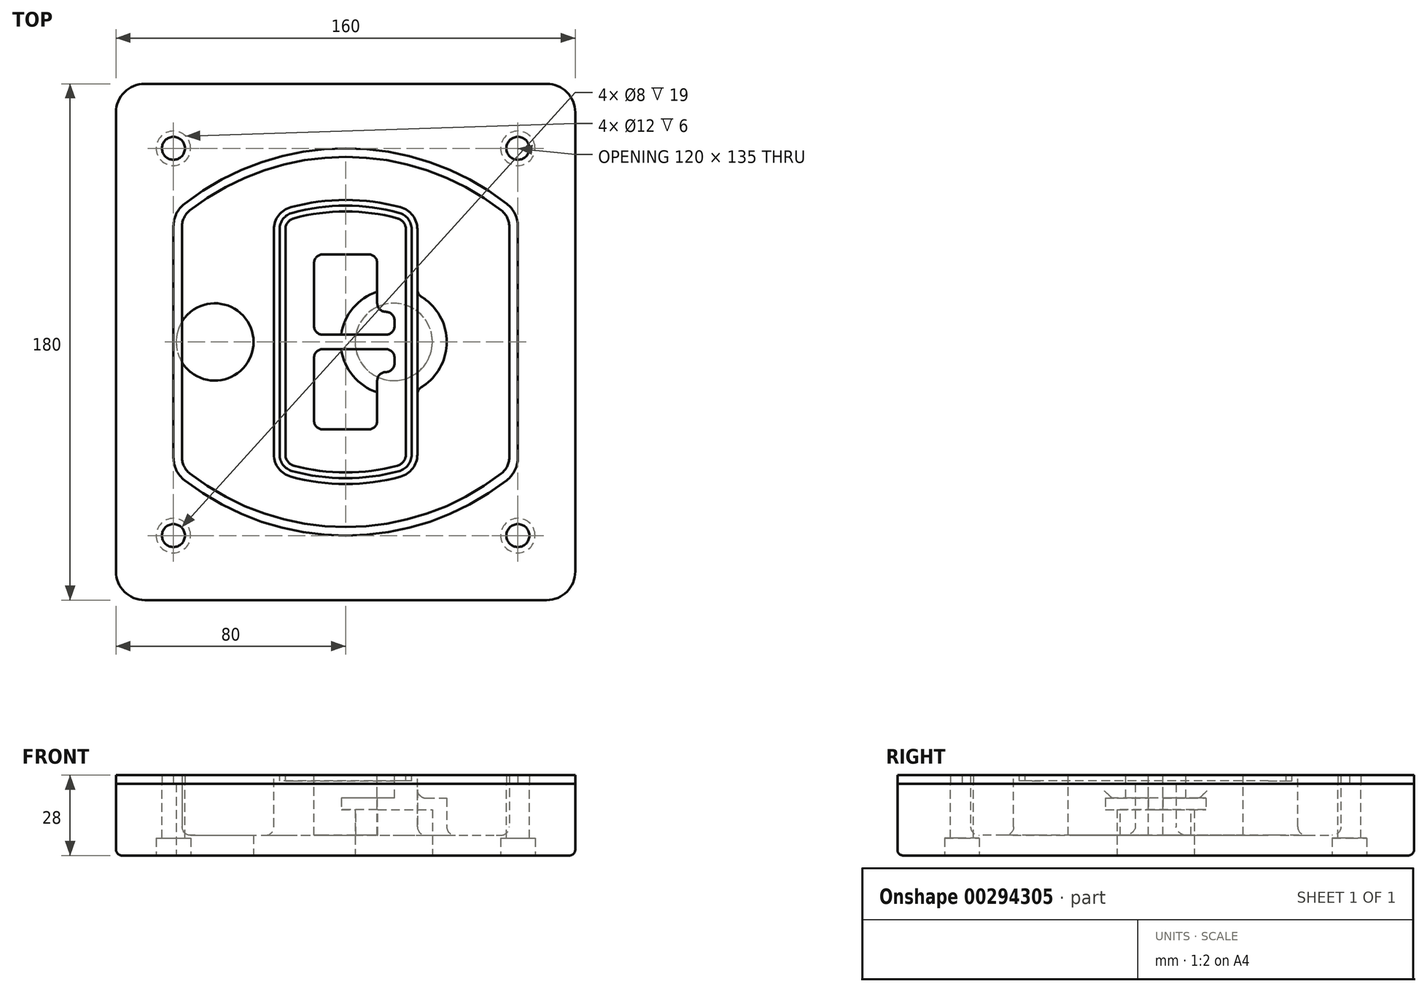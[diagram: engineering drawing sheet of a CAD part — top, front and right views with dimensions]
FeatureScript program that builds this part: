
annotation { "Feature Type Name" : "Feature", "Feature Type Description" : "" }
export const myFeature = defineFeature(function(context is Context, id is Id, definition is map)
    precondition{}
    {
        {
            var Q0;
            Q0=qCreatedBy(makeId("Top.planeOp"),FACE);
            var sketch = newSketch(context, id + "F0", { "sketchPlane" : qUnion([Q0])});
            skPoint(sketch, "E0.rect.middle", {"position": v(0, 0) * mm});
            skLineSegment(sketch, "E1.bottom", {"start": v(-70, -90) * mm, "end": v(70, -90) * mm});
            skLineSegment(sketch, "E1.top", {"start": v(-70, 90) * mm, "end": v(70, 90) * mm});
            skLineSegment(sketch, "E1.left", {"start": v(-80, -80) * mm, "end": v(-80, 80) * mm});
            skLineSegment(sketch, "E1.right", {"start": v(80, -80) * mm, "end": v(80, 80) * mm});
            skLineSegment(sketch, "E2", {"start": v(-80, 90) * mm, "end": v(80, -90) * mm, "construction": true});
            skLineSegment(sketch, "E3", {"start": v(80, 90) * mm, "end": v(-80, -90) * mm, "construction": true});
            skCircle(sketch, "E4", {"center": v(-60, 67.5) * mm, "radius": 4 * mm});
            skCircle(sketch, "E5", {"center": v(60, 67.5) * mm, "radius": 4 * mm});
            skCircle(sketch, "E6", {"center": v(60, -67.5) * mm, "radius": 4 * mm});
            skCircle(sketch, "E7", {"center": v(-60, -67.5) * mm, "radius": 4 * mm});
            skLineSegment(sketch, "E8", {"start": v(-60, 67.5) * mm, "end": v(60, 67.5) * mm, "construction": true});
            skLineSegment(sketch, "E9", {"start": v(60, 67.5) * mm, "end": v(60, -67.5) * mm, "construction": true});
            skLineSegment(sketch, "E10", {"start": v(60, -67.5) * mm, "end": v(-60, -67.5) * mm, "construction": true});
            skLineSegment(sketch, "E11", {"start": v(-60, -67.5) * mm, "end": v(-60, 67.5) * mm, "construction": true});
            skLineSegment(sketch, "E12", {"start": v(-60, 40.3) * mm, "end": v(-60, -40.3) * mm});
            skLineSegment(sketch, "E13", {"start": v(60, 40.3) * mm, "end": v(60, -40.3) * mm});
            skArc(sketch, "E14", {"start": v(56.15, 48.18) * mm, "mid": v(0, 67.5) * mm, "end": v(-56.15, 48.18) * mm});
            skArc(sketch, "E15", {"start": v(-56.15, -48.18) * mm, "mid": v(0, -67.5) * mm, "end": v(56.15, -48.18) * mm});
            skLineSegment(sketch, "E16", {"start": v(-60, 0) * mm, "end": v(60, 0) * mm, "construction": true});
            skPoint(sketch, "E17.visualSharp", {"position": v(-60, -45) * mm});
            skArc(sketch, "E17.filletArc", {"start": v(-60, -40.3) * mm, "mid": v(-58.99, -44.68) * mm, "end": v(-56.15, -48.18) * mm});
            skPoint(sketch, "E18.visualSharp", {"position": v(-60, 45) * mm});
            skArc(sketch, "E18.filletArc", {"start": v(-56.15, 48.18) * mm, "mid": v(-58.99, 44.68) * mm, "end": v(-60, 40.3) * mm});
            skPoint(sketch, "E19.visualSharp", {"position": v(60, 45) * mm});
            skArc(sketch, "E19.filletArc", {"start": v(60, 40.3) * mm, "mid": v(58.99, 44.68) * mm, "end": v(56.15, 48.18) * mm});
            skPoint(sketch, "E20.visualSharp", {"position": v(60, -45) * mm});
            skArc(sketch, "E20.filletArc", {"start": v(56.15, -48.18) * mm, "mid": v(58.99, -44.68) * mm, "end": v(60, -40.3) * mm});
            skPoint(sketch, "E21.visualSharp", {"position": v(-80, 90) * mm});
            skArc(sketch, "E21.filletArc", {"start": v(-70, 90) * mm, "mid": v(-77.07, 87.07) * mm, "end": v(-80, 80) * mm});
            skPoint(sketch, "E22.visualSharp", {"position": v(80, 90) * mm});
            skArc(sketch, "E22.filletArc", {"start": v(80, 80) * mm, "mid": v(77.07, 87.07) * mm, "end": v(70, 90) * mm});
            skPoint(sketch, "E23.visualSharp", {"position": v(80, -90) * mm});
            skArc(sketch, "E23.filletArc", {"start": v(70, -90) * mm, "mid": v(77.07, -87.07) * mm, "end": v(80, -80) * mm});
            skPoint(sketch, "E24.visualSharp", {"position": v(-80, -90) * mm});
            skArc(sketch, "E24.filletArc", {"start": v(-80, -80) * mm, "mid": v(-77.07, -87.07) * mm, "end": v(-70, -90) * mm});
            skArc(sketch, "E25.0", {"start": v(57, 40.3) * mm, "mid": v(56.3, 43.36) * mm, "end": v(54.3, 45.81) * mm});
            skLineSegment(sketch, "E25.1", {"start": v(57, 40.3) * mm, "end": v(57, -40.3) * mm});
            skArc(sketch, "E25.2", {"start": v(54.3, -45.81) * mm, "mid": v(56.3, -43.36) * mm, "end": v(57, -40.3) * mm});
            skArc(sketch, "E25.3", {"start": v(-54.3, -45.81) * mm, "mid": v(0, -64.5) * mm, "end": v(54.3, -45.81) * mm});
            skArc(sketch, "E25.4", {"start": v(-57, -40.3) * mm, "mid": v(-56.3, -43.36) * mm, "end": v(-54.3, -45.81) * mm});
            skArc(sketch, "E25.5", {"start": v(54.3, 45.81) * mm, "mid": v(0, 64.5) * mm, "end": v(-54.3, 45.81) * mm});
            skLineSegment(sketch, "E25.6", {"start": v(-57, 40.3) * mm, "end": v(-57, -40.3) * mm});
            skArc(sketch, "E25.7", {"start": v(-54.3, 45.81) * mm, "mid": v(-56.3, 43.36) * mm, "end": v(-57, 40.3) * mm});
            skArc(sketch, "E26.0", {"start": v(-58.62, 51.33) * mm, "mid": v(-62.58, 46.43) * mm, "end": v(-64, 40.3) * mm});
            skArc(sketch, "E26.1", {"start": v(58.62, 51.33) * mm, "mid": v(0, 71.5) * mm, "end": v(-58.62, 51.33) * mm});
            skArc(sketch, "E26.2", {"start": v(64, 40.3) * mm, "mid": v(62.58, 46.43) * mm, "end": v(58.62, 51.33) * mm});
            skLineSegment(sketch, "E26.3", {"start": v(64, 40.3) * mm, "end": v(64, -40.3) * mm});
            skArc(sketch, "E26.4", {"start": v(58.62, -51.33) * mm, "mid": v(62.58, -46.43) * mm, "end": v(64, -40.3) * mm});
            skLineSegment(sketch, "E26.5", {"start": v(-64, 40.3) * mm, "end": v(-64, -40.3) * mm});
            skArc(sketch, "E26.6", {"start": v(-58.62, -51.33) * mm, "mid": v(0, -71.5) * mm, "end": v(58.62, -51.33) * mm});
            skArc(sketch, "E26.7", {"start": v(-64, -40.3) * mm, "mid": v(-62.58, -46.43) * mm, "end": v(-58.62, -51.33) * mm});
            skSolve(sketch);
        }
        {
            var Q0;
            Q0=makeQuery(id+"F0.imprint","IMPRINT",FACE,{"disambiguationData":[TD([[makeQuery(id+"F0.imprint","IMPRINT",EDGE,{"derivedFrom":sQuery(id+"F0.wireOp",EDGE,"E1.bottom")}),1.0]])]});
            var Q1;
            Q1=makeQuery(id+"F0.imprint","IMPRINT",FACE,{"disambiguationData":[TD([[makeQuery(id+"F0.imprint","IMPRINT",EDGE,{"derivedFrom":sQuery(id+"F0.wireOp",EDGE,"E12")}),1.0]])]});
            var Q2;
            Q2=makeQuery(id+"F0.imprint","IMPRINT",FACE,{"disambiguationData":[TD([[makeQuery(id+"F0.imprint","IMPRINT",EDGE,{"derivedFrom":sQuery(id+"F0.wireOp",EDGE,"E25.0")}),1.0]])]});
            var Q3;
            Q3=makeQuery(id+"F0.imprint","IMPRINT",FACE,{"disambiguationData":[TD([[makeQuery(id+"F0.imprint","IMPRINT",EDGE,{"derivedFrom":sQuery(id+"F0.wireOp",EDGE,"E12")}),-1.0]])]});
            extrude(context, id + "F1", {"entities" : qUnion([Q0, Q1, Q2, Q3]), "oppositeDirection" : true, "depth" : 25 * mm});
        }
        {
            var Q0;
            Q0=makeQuery(id+"F0.imprint","IMPRINT",FACE,{"disambiguationData":[TD([[makeQuery(id+"F0.imprint","IMPRINT",EDGE,{"derivedFrom":sQuery(id+"F0.wireOp",EDGE,"E12")}),1.0]])]});
            extrude(context, id + "F2", {"entities" : qUnion([Q0]), "operationType" : NewBodyOperationType.ADD, "depth" : 3 * mm});
        }
        {
            var Q0;
            Q0=makeQuery(id+"F0.imprint","IMPRINT",FACE,{"disambiguationData":[TD([[makeQuery(id+"F0.imprint","IMPRINT",EDGE,{"derivedFrom":sQuery(id+"F0.wireOp",EDGE,"E25.0")}),1.0]])]});
            extrude(context, id + "F3", {"entities" : qUnion([Q0]), "operationType" : NewBodyOperationType.REMOVE, "oppositeDirection" : true, "depth" : 18 * mm});
        }
        {
            var Q0;
            Q0=makeQuery(id+"F2.opExtrude","CAP_FACE",FACE,{"disambiguationData":[OSD([sQuery(id+"F0.wireOp",EDGE,"E12"),sQuery(id+"F0.wireOp",EDGE,"E13"),sQuery(id+"F0.wireOp",EDGE,"E14"),sQuery(id+"F0.wireOp",EDGE,"E15"),sQuery(id+"F0.wireOp",EDGE,"E17.filletArc"),sQuery(id+"F0.wireOp",EDGE,"E18.filletArc"),sQuery(id+"F0.wireOp",EDGE,"E19.filletArc"),sQuery(id+"F0.wireOp",EDGE,"E20.filletArc"),sQuery(id+"F0.wireOp",EDGE,"E25.0"),sQuery(id+"F0.wireOp",EDGE,"E25.1"),sQuery(id+"F0.wireOp",EDGE,"E25.2"),sQuery(id+"F0.wireOp",EDGE,"E25.3"),sQuery(id+"F0.wireOp",EDGE,"E25.4"),sQuery(id+"F0.wireOp",EDGE,"E25.5"),sQuery(id+"F0.wireOp",EDGE,"E25.6"),sQuery(id+"F0.wireOp",EDGE,"E25.7")])],"isStart":false});
            var sketch = newSketch(context, id + "F4", { "sketchPlane" : qUnion([Q0])});
            skArc(sketch, "E27.0", {"start": v(-19.08, -46.97) * mm, "mid": v(0, -49.5) * mm, "end": v(19.08, -46.97) * mm});
            skArc(sketch, "E28.0", {"start": v(19.08, 46.97) * mm, "mid": v(0, 49.5) * mm, "end": v(-19.08, 46.97) * mm});
            skLineSegment(sketch, "E29", {"start": v(-25, 39.25) * mm, "end": v(-25, -39.25) * mm});
            skLineSegment(sketch, "E30", {"start": v(25, 39.25) * mm, "end": v(25, -39.25) * mm});
            skLineSegment(sketch, "E31", {"start": v(-25, 45.1) * mm, "end": v(25, 45.1) * mm, "construction": true});
            skLineSegment(sketch, "E32", {"start": v(-25, -45.1) * mm, "end": v(25, -45.1) * mm, "construction": true});
            skPoint(sketch, "E33.visualSharp", {"position": v(-25, 45.1) * mm});
            skArc(sketch, "E33.filletArc", {"start": v(-19.08, 46.97) * mm, "mid": v(-23.35, 44.11) * mm, "end": v(-25, 39.25) * mm});
            skPoint(sketch, "E34.visualSharp", {"position": v(25, 45.1) * mm});
            skArc(sketch, "E34.filletArc", {"start": v(25, 39.25) * mm, "mid": v(23.35, 44.11) * mm, "end": v(19.08, 46.97) * mm});
            skPoint(sketch, "E35.visualSharp", {"position": v(25, -45.1) * mm});
            skArc(sketch, "E35.filletArc", {"start": v(19.08, -46.97) * mm, "mid": v(23.35, -44.11) * mm, "end": v(25, -39.25) * mm});
            skPoint(sketch, "E36.visualSharp", {"position": v(-25, -45.1) * mm});
            skArc(sketch, "E36.filletArc", {"start": v(-25, -39.25) * mm, "mid": v(-23.35, -44.11) * mm, "end": v(-19.08, -46.97) * mm});
            skArc(sketch, "E37.0", {"start": v(54.3, 45.81) * mm, "mid": v(0, 64.5) * mm, "end": v(-54.3, 45.81) * mm});
            skArc(sketch, "E37.1", {"start": v(-54.3, 45.81) * mm, "mid": v(-56.3, 43.36) * mm, "end": v(-57, 40.3) * mm});
            skLineSegment(sketch, "E37.2", {"start": v(-57, 40.3) * mm, "end": v(-57, -40.3) * mm});
            skArc(sketch, "E37.3", {"start": v(-57, -40.3) * mm, "mid": v(-56.3, -43.36) * mm, "end": v(-54.3, -45.81) * mm});
            skArc(sketch, "E37.4", {"start": v(-54.3, -45.81) * mm, "mid": v(0, -64.5) * mm, "end": v(54.3, -45.81) * mm});
            skArc(sketch, "E37.5", {"start": v(54.3, -45.81) * mm, "mid": v(56.3, -43.36) * mm, "end": v(57, -40.3) * mm});
            skLineSegment(sketch, "E37.6", {"start": v(57, 40.3) * mm, "end": v(57, -40.3) * mm});
            skArc(sketch, "E37.7", {"start": v(57, 40.3) * mm, "mid": v(56.3, 43.36) * mm, "end": v(54.3, 45.81) * mm});
            skLineSegment(sketch, "E38.0", {"start": v(23, 39.25) * mm, "end": v(23, -39.25) * mm});
            skArc(sketch, "E38.1", {"start": v(18.56, -45.04) * mm, "mid": v(21.76, -42.9) * mm, "end": v(23, -39.25) * mm});
            skArc(sketch, "E38.2", {"start": v(-18.56, -45.04) * mm, "mid": v(0, -47.5) * mm, "end": v(18.56, -45.04) * mm});
            skArc(sketch, "E38.3", {"start": v(-23, -39.25) * mm, "mid": v(-21.76, -42.9) * mm, "end": v(-18.56, -45.04) * mm});
            skLineSegment(sketch, "E38.4", {"start": v(-23, 39.25) * mm, "end": v(-23, -39.25) * mm});
            skArc(sketch, "E38.5", {"start": v(23, 39.25) * mm, "mid": v(21.76, 42.9) * mm, "end": v(18.56, 45.04) * mm});
            skArc(sketch, "E38.6", {"start": v(-18.56, 45.04) * mm, "mid": v(-21.76, 42.9) * mm, "end": v(-23, 39.25) * mm});
            skArc(sketch, "E38.7", {"start": v(18.56, 45.04) * mm, "mid": v(0, 47.5) * mm, "end": v(-18.56, 45.04) * mm});
            skArc(sketch, "E39.0", {"start": v(21, 39.25) * mm, "mid": v(20.18, 41.68) * mm, "end": v(18.04, 43.1) * mm});
            skLineSegment(sketch, "E39.1", {"start": v(21, 39.25) * mm, "end": v(21, -39.25) * mm});
            skArc(sketch, "E39.2", {"start": v(18.04, -43.1) * mm, "mid": v(20.18, -41.68) * mm, "end": v(21, -39.25) * mm});
            skArc(sketch, "E39.3", {"start": v(-18.04, -43.1) * mm, "mid": v(0, -45.5) * mm, "end": v(18.04, -43.1) * mm});
            skArc(sketch, "E39.4", {"start": v(-21, -39.25) * mm, "mid": v(-20.18, -41.68) * mm, "end": v(-18.04, -43.1) * mm});
            skArc(sketch, "E39.5", {"start": v(18.04, 43.1) * mm, "mid": v(0, 45.5) * mm, "end": v(-18.04, 43.1) * mm});
            skLineSegment(sketch, "E39.6", {"start": v(-21, 39.25) * mm, "end": v(-21, -39.25) * mm});
            skArc(sketch, "E39.7", {"start": v(-18.04, 43.1) * mm, "mid": v(-20.18, 41.68) * mm, "end": v(-21, 39.25) * mm});
            skLineSegment(sketch, "E40", {"start": v(-25, 0) * mm, "end": v(25, 0) * mm, "construction": true});
            skLineSegment(sketch, "E41", {"start": v(-11, 5.5) * mm, "end": v(-11, 27.5) * mm});
            skLineSegment(sketch, "E42", {"start": v(-8, 30.5) * mm, "end": v(8, 30.5) * mm});
            skLineSegment(sketch, "E43", {"start": v(11, 27.5) * mm, "end": v(11, 13.5) * mm});
            skLineSegment(sketch, "E44", {"start": v(14, 10.5) * mm, "end": v(14, 10.5) * mm});
            skLineSegment(sketch, "E45", {"start": v(17, 7.5) * mm, "end": v(17, 5.5) * mm});
            skLineSegment(sketch, "E46", {"start": v(14, 2.5) * mm, "end": v(-8, 2.5) * mm});
            skPoint(sketch, "E47.visualSharp", {"position": v(-11, 30.5) * mm});
            skArc(sketch, "E47.filletArc", {"start": v(-8, 30.5) * mm, "mid": v(-10.12, 29.62) * mm, "end": v(-11, 27.5) * mm});
            skPoint(sketch, "E48.visualSharp", {"position": v(11, 30.5) * mm});
            skArc(sketch, "E48.filletArc", {"start": v(11, 27.5) * mm, "mid": v(10.12, 29.62) * mm, "end": v(8, 30.5) * mm});
            skPoint(sketch, "E49.visualSharp", {"position": v(11, 10.5) * mm});
            skArc(sketch, "E49.filletArc", {"start": v(11, 13.5) * mm, "mid": v(11.88, 11.38) * mm, "end": v(14, 10.5) * mm});
            skPoint(sketch, "E50.visualSharp", {"position": v(17, 10.5) * mm});
            skArc(sketch, "E50.filletArc", {"start": v(17, 7.5) * mm, "mid": v(16.12, 9.62) * mm, "end": v(14, 10.5) * mm});
            skPoint(sketch, "E51.visualSharp", {"position": v(17, 2.5) * mm});
            skArc(sketch, "E51.filletArc", {"start": v(14, 2.5) * mm, "mid": v(16.12, 3.38) * mm, "end": v(17, 5.5) * mm});
            skPoint(sketch, "E52.visualSharp", {"position": v(-11, 2.5) * mm});
            skArc(sketch, "E52.filletArc", {"start": v(-11, 5.5) * mm, "mid": v(-10.12, 3.38) * mm, "end": v(-8, 2.5) * mm});
            skLineSegment(sketch, "E53.0.MirrorCS", {"start": v(14, -2.5) * mm, "end": v(-8, -2.5) * mm});
            skArc(sketch, "E54.0.MirrorCS", {"start": v(-11, -5.5) * mm, "mid": v(-10.12, -3.38) * mm, "end": v(-8, -2.5) * mm});
            skLineSegment(sketch, "E55.0.MirrorCS", {"start": v(-11, -5.5) * mm, "end": v(-11, -27.5) * mm});
            skArc(sketch, "E56.0.MirrorCS", {"start": v(-8, -30.5) * mm, "mid": v(-10.12, -29.62) * mm, "end": v(-11, -27.5) * mm});
            skLineSegment(sketch, "E57.0.MirrorCS", {"start": v(-8, -30.5) * mm, "end": v(8, -30.5) * mm});
            skArc(sketch, "E58.0.MirrorCS", {"start": v(11, -27.5) * mm, "mid": v(10.12, -29.62) * mm, "end": v(8, -30.5) * mm});
            skLineSegment(sketch, "E59.0.MirrorCS", {"start": v(11, -27.5) * mm, "end": v(11, -13.5) * mm});
            skArc(sketch, "E60.0.MirrorCS", {"start": v(11, -13.5) * mm, "mid": v(11.88, -11.38) * mm, "end": v(14, -10.5) * mm});
            skArc(sketch, "E61.0.MirrorCS", {"start": v(17, -7.5) * mm, "mid": v(16.12, -9.62) * mm, "end": v(14, -10.5) * mm});
            skLineSegment(sketch, "E62.0.MirrorCS", {"start": v(17, -7.5) * mm, "end": v(17, -5.5) * mm});
            skArc(sketch, "E63.0.MirrorCS", {"start": v(14, -2.5) * mm, "mid": v(16.12, -3.38) * mm, "end": v(17, -5.5) * mm});
            skSolve(sketch);
        }
        {
            var Q0;
            Q0=makeQuery(id+"F4.imprint","IMPRINT",FACE,{"disambiguationData":[TD([[makeQuery(id+"F4.imprint","IMPRINT",EDGE,{"derivedFrom":sQuery(id+"F4.wireOp",EDGE,"E27.0")}),1.0]])]});
            var Q1;
            Q1=makeQuery(id+"F4.imprint","IMPRINT",FACE,{"disambiguationData":[TD([[makeQuery(id+"F4.imprint","IMPRINT",EDGE,{"derivedFrom":sQuery(id+"F4.wireOp",EDGE,"E38.0")}),-1.0]])]});
            var Q2;
            Q2=makeQuery(id+"F4.imprint","IMPRINT",FACE,{"disambiguationData":[TD([[makeQuery(id+"F4.imprint","IMPRINT",EDGE,{"derivedFrom":sQuery(id+"F4.wireOp",EDGE,"E39.0")}),1.0]])]});
            extrude(context, id + "F5", {"entities" : qUnion([Q0, Q1, Q2]), "operationType" : NewBodyOperationType.ADD, "endBound" : BoundingType.UP_TO_NEXT, "oppositeDirection" : true, "depth" : 25 * mm});
        }
        {
            var Q0;
            Q0=makeQuery(id+"F4.imprint","IMPRINT",FACE,{"disambiguationData":[TD([[makeQuery(id+"F4.imprint","IMPRINT",EDGE,{"derivedFrom":sQuery(id+"F4.wireOp",EDGE,"E38.0")}),-1.0]])]});
            extrude(context, id + "F6", {"entities" : qUnion([Q0]), "operationType" : NewBodyOperationType.REMOVE, "oppositeDirection" : true, "depth" : 2 * mm});
        }
        {
            var Q0;
            Q0=makeQuery(id+"F1.opExtrude","CAP_FACE",FACE,{"disambiguationData":[OSD([sQuery(id+"F0.wireOp",EDGE,"E1.bottom"),sQuery(id+"F0.wireOp",EDGE,"E1.top"),sQuery(id+"F0.wireOp",EDGE,"E1.left"),sQuery(id+"F0.wireOp",EDGE,"E1.right"),sQuery(id+"F0.wireOp",EDGE,"E4"),sQuery(id+"F0.wireOp",EDGE,"E5"),sQuery(id+"F0.wireOp",EDGE,"E6"),sQuery(id+"F0.wireOp",EDGE,"E7"),sQuery(id+"F0.wireOp",EDGE,"E21.filletArc"),sQuery(id+"F0.wireOp",EDGE,"E22.filletArc"),sQuery(id+"F0.wireOp",EDGE,"E23.filletArc"),sQuery(id+"F0.wireOp",EDGE,"E24.filletArc")])],"isStart":false});
            var sketch = newSketch(context, id + "F7", { "sketchPlane" : qUnion([Q0])});
            skCircle(sketch, "E64", {"center": v(16.76, 0) * mm, "radius": 13.47 * mm});
            skCircle(sketch, "E65", {"center": v(-45.56, 0) * mm, "radius": 13.47 * mm});
            skLineSegment(sketch, "E66", {"start": v(80, 0) * mm, "end": v(-80, 0) * mm});
            skCircle(sketch, "E67", {"center": v(16.76, 0) * mm, "radius": 18.47 * mm});
            skCircle(sketch, "E68", {"center": v(60, -67.5) * mm, "radius": 6 * mm});
            skCircle(sketch, "E69", {"center": v(-60, -67.5) * mm, "radius": 6 * mm});
            skCircle(sketch, "E70", {"center": v(-60, 67.5) * mm, "radius": 6 * mm});
            skCircle(sketch, "E71", {"center": v(60, 67.5) * mm, "radius": 6 * mm});
            skSolve(sketch);
        }
        {
            var Q0;
            {var subQ1=sQuery(id+"F7.wireOp",EDGE,"E66");var subQ4=sQuery(id+"F7.wireOp",EDGE,"E64");var subQ6=makeQuery(id+"F7.imprint","INTERSECT",VERTEX,{"disambiguationData":[OD(0.0)],"derivedFrom":[subQ4,subQ1]});Q0=makeQuery(id+"F7.imprint","IMPRINT",FACE,{"disambiguationData":[TD([[makeQuery(id+"F7.imprint","IMPRINT",EDGE,{"disambiguationData":[TD([[subQ6,-1.0]])],"derivedFrom":subQ4}),-1.0]])]});}
            var Q1;
            {var subQ0=sQuery(id+"F7.wireOp",EDGE,"E66");var subQ1=sQuery(id+"F7.wireOp",EDGE,"E64");var subQ3=makeQuery(id+"F7.imprint","INTERSECT",VERTEX,{"disambiguationData":[OD(0.0)],"derivedFrom":[subQ1,subQ0]});Q1=makeQuery(id+"F7.imprint","IMPRINT",FACE,{"disambiguationData":[TD([[makeQuery(id+"F7.imprint","IMPRINT",EDGE,{"disambiguationData":[TD([[subQ3,-1.0]])],"derivedFrom":subQ1}),1.0]])]});}
            var Q2;
            {var subQ0=sQuery(id+"F7.wireOp",EDGE,"E66");var subQ1=sQuery(id+"F7.wireOp",EDGE,"E64");var subQ3=makeQuery(id+"F7.imprint","INTERSECT",VERTEX,{"disambiguationData":[OD(0.0)],"derivedFrom":[subQ1,subQ0]});Q2=makeQuery(id+"F7.imprint","IMPRINT",FACE,{"disambiguationData":[TD([[makeQuery(id+"F7.imprint","IMPRINT",EDGE,{"disambiguationData":[TD([[subQ3,1.0]])],"derivedFrom":subQ1}),1.0]])]});}
            var Q3;
            {var subQ1=sQuery(id+"F7.wireOp",EDGE,"E66");var subQ4=sQuery(id+"F7.wireOp",EDGE,"E64");var subQ6=makeQuery(id+"F7.imprint","INTERSECT",VERTEX,{"disambiguationData":[OD(0.0)],"derivedFrom":[subQ4,subQ1]});Q3=makeQuery(id+"F7.imprint","IMPRINT",FACE,{"disambiguationData":[TD([[makeQuery(id+"F7.imprint","IMPRINT",EDGE,{"disambiguationData":[TD([[subQ6,1.0]])],"derivedFrom":subQ4}),-1.0]])]});}
            extrude(context, id + "F8", {"entities" : qUnion([Q0, Q1, Q2, Q3]), "operationType" : NewBodyOperationType.ADD, "oppositeDirection" : true, "depth" : 20 * mm});
        }
        {
            var Q0;
            {var subQ0=sQuery(id+"F7.wireOp",EDGE,"E66");var subQ1=sQuery(id+"F7.wireOp",EDGE,"E64");var subQ3=makeQuery(id+"F7.imprint","INTERSECT",VERTEX,{"disambiguationData":[OD(0.0)],"derivedFrom":[subQ1,subQ0]});Q0=makeQuery(id+"F7.imprint","IMPRINT",FACE,{"disambiguationData":[TD([[makeQuery(id+"F7.imprint","IMPRINT",EDGE,{"disambiguationData":[TD([[subQ3,-1.0]])],"derivedFrom":subQ1}),1.0]])]});}
            var Q1;
            {var subQ0=sQuery(id+"F7.wireOp",EDGE,"E66");var subQ1=sQuery(id+"F7.wireOp",EDGE,"E64");var subQ3=makeQuery(id+"F7.imprint","INTERSECT",VERTEX,{"disambiguationData":[OD(0.0)],"derivedFrom":[subQ1,subQ0]});Q1=makeQuery(id+"F7.imprint","IMPRINT",FACE,{"disambiguationData":[TD([[makeQuery(id+"F7.imprint","IMPRINT",EDGE,{"disambiguationData":[TD([[subQ3,1.0]])],"derivedFrom":subQ1}),1.0]])]});}
            extrude(context, id + "F9", {"entities" : qUnion([Q0, Q1]), "operationType" : NewBodyOperationType.REMOVE, "oppositeDirection" : true, "depth" : 16 * mm});
        }
        {
            var Q0;
            {var subQ0=sQuery(id+"F7.wireOp",EDGE,"E66");var subQ1=sQuery(id+"F7.wireOp",EDGE,"E65");var subQ3=makeQuery(id+"F7.imprint","INTERSECT",VERTEX,{"disambiguationData":[OD(0.0)],"derivedFrom":[subQ1,subQ0]});Q0=makeQuery(id+"F7.imprint","IMPRINT",FACE,{"disambiguationData":[TD([[makeQuery(id+"F7.imprint","IMPRINT",EDGE,{"disambiguationData":[TD([[subQ3,-1.0]])],"derivedFrom":subQ1}),1.0]])]});}
            var Q1;
            {var subQ0=sQuery(id+"F7.wireOp",EDGE,"E66");var subQ1=sQuery(id+"F7.wireOp",EDGE,"E65");var subQ3=makeQuery(id+"F7.imprint","INTERSECT",VERTEX,{"disambiguationData":[OD(0.0)],"derivedFrom":[subQ1,subQ0]});Q1=makeQuery(id+"F7.imprint","IMPRINT",FACE,{"disambiguationData":[TD([[makeQuery(id+"F7.imprint","IMPRINT",EDGE,{"disambiguationData":[TD([[subQ3,1.0]])],"derivedFrom":subQ1}),1.0]])]});}
            extrude(context, id + "F10", {"entities" : qUnion([Q0, Q1]), "operationType" : NewBodyOperationType.REMOVE, "oppositeDirection" : true, "depth" : 25 * mm});
        }
        {
            var Q0;
            Q0=makeQuery(id+"F7.imprint","IMPRINT",FACE,{"disambiguationData":[TD([[makeQuery(id+"F7.imprint","IMPRINT",EDGE,{"derivedFrom":sQuery(id+"F7.wireOp",EDGE,"E68")}),1.0]])]});
            var Q1;
            Q1=makeQuery(id+"F7.imprint","IMPRINT",FACE,{"disambiguationData":[TD([[makeQuery(id+"F7.imprint","IMPRINT",EDGE,{"derivedFrom":makeQuery(id+"F1.opExtrude","CAP_EDGE",EDGE,{"disambiguationData":[OSD([sQuery(id+"F0.wireOp",EDGE,"E5")])],"isStart":false})}),-1.0]])]});
            var Q2;
            Q2=makeQuery(id+"F7.imprint","IMPRINT",FACE,{"disambiguationData":[TD([[makeQuery(id+"F7.imprint","IMPRINT",EDGE,{"derivedFrom":sQuery(id+"F7.wireOp",EDGE,"E69")}),1.0]])]});
            var Q3;
            Q3=makeQuery(id+"F7.imprint","IMPRINT",FACE,{"disambiguationData":[TD([[makeQuery(id+"F7.imprint","IMPRINT",EDGE,{"derivedFrom":makeQuery(id+"F1.opExtrude","CAP_EDGE",EDGE,{"disambiguationData":[OSD([sQuery(id+"F0.wireOp",EDGE,"E4")])],"isStart":false})}),-1.0]])]});
            var Q4;
            Q4=makeQuery(id+"F7.imprint","IMPRINT",FACE,{"disambiguationData":[TD([[makeQuery(id+"F7.imprint","IMPRINT",EDGE,{"derivedFrom":sQuery(id+"F7.wireOp",EDGE,"E70")}),1.0]])]});
            var Q5;
            Q5=makeQuery(id+"F7.imprint","IMPRINT",FACE,{"disambiguationData":[TD([[makeQuery(id+"F7.imprint","IMPRINT",EDGE,{"derivedFrom":makeQuery(id+"F1.opExtrude","CAP_EDGE",EDGE,{"disambiguationData":[OSD([sQuery(id+"F0.wireOp",EDGE,"E7")])],"isStart":false})}),-1.0]])]});
            var Q6;
            Q6=makeQuery(id+"F7.imprint","IMPRINT",FACE,{"disambiguationData":[TD([[makeQuery(id+"F7.imprint","IMPRINT",EDGE,{"derivedFrom":sQuery(id+"F7.wireOp",EDGE,"E71")}),1.0]])]});
            var Q7;
            Q7=makeQuery(id+"F7.imprint","IMPRINT",FACE,{"disambiguationData":[TD([[makeQuery(id+"F7.imprint","IMPRINT",EDGE,{"derivedFrom":makeQuery(id+"F1.opExtrude","CAP_EDGE",EDGE,{"disambiguationData":[OSD([sQuery(id+"F0.wireOp",EDGE,"E6")])],"isStart":false})}),-1.0]])]});
            extrude(context, id + "F11", {"entities" : qUnion([Q0, Q1, Q2, Q3, Q4, Q5, Q6, Q7]), "operationType" : NewBodyOperationType.REMOVE, "oppositeDirection" : true, "depth" : 6 * mm});
        }
        {
            var Q0;
            Q0=makeQuery(id+"F9.boolean.opBoolean","COPY",FACE,{"derivedFrom":makeQuery(id+"F9.opExtrude","CAP_FACE",FACE,{"disambiguationData":[OSD([sQuery(id+"F7.wireOp",EDGE,"E64")])],"isStart":false})});
            var sketch = newSketch(context, id + "F12", { "sketchPlane" : qUnion([Q0])});
            skArc(sketch, "E72.0", {"start": v(11, 17.55) * mm, "mid": v(2.57, 11.82) * mm, "end": v(-1.54, 2.5) * mm});
            skArc(sketch, "E72.1", {"start": v(-1.54, -2.5) * mm, "mid": v(2.57, -11.82) * mm, "end": v(11, -17.55) * mm});
            skLineSegment(sketch, "E73", {"start": v(-1.54, -2.5) * mm, "end": v(14, -2.5) * mm});
            skLineSegment(sketch, "E74.0", {"start": v(14, 2.5) * mm, "end": v(-1.54, 2.5) * mm});
            skArc(sketch, "E74.1", {"start": v(14, 2.5) * mm, "mid": v(16.12, 3.38) * mm, "end": v(17, 5.5) * mm});
            skLineSegment(sketch, "E74.2", {"start": v(17, 7.5) * mm, "end": v(17, 5.5) * mm});
            skArc(sketch, "E74.3", {"start": v(17, 7.5) * mm, "mid": v(16.12, 9.62) * mm, "end": v(14, 10.5) * mm});
            skArc(sketch, "E74.4", {"start": v(11, 13.5) * mm, "mid": v(11.88, 11.38) * mm, "end": v(14, 10.5) * mm});
            skLineSegment(sketch, "E74.5", {"start": v(11, 17.55) * mm, "end": v(11, 13.5) * mm});
            skLineSegment(sketch, "E74.7", {"start": v(14, -2.5) * mm, "end": v(-1.54, -2.5) * mm});
            skArc(sketch, "E74.8", {"start": v(14, -2.5) * mm, "mid": v(16.12, -3.38) * mm, "end": v(17, -5.5) * mm});
            skLineSegment(sketch, "E74.9", {"start": v(17, -7.5) * mm, "end": v(17, -5.5) * mm});
            skArc(sketch, "E74.10", {"start": v(17, -7.5) * mm, "mid": v(16.12, -9.62) * mm, "end": v(14, -10.5) * mm});
            skArc(sketch, "E74.11", {"start": v(11, -13.5) * mm, "mid": v(11.88, -11.38) * mm, "end": v(14, -10.5) * mm});
            skLineSegment(sketch, "E74.12", {"start": v(11, -17.55) * mm, "end": v(11, -13.5) * mm});
            skPoint(sketch, "E75.orphan", {"position": v(11, -27.5) * mm});
            skPoint(sketch, "E76.orphan", {"position": v(-8, -2.5) * mm});
            skPoint(sketch, "E77.orphan", {"position": v(-8, 2.5) * mm});
            skPoint(sketch, "E78.orphan", {"position": v(11, 27.5) * mm});
            skSolve(sketch);
        }
        {
            var Q0;
            {var subQ7=sQuery(id+"F12.wireOp",EDGE,"E72.0");var subQ14=sQuery(id+"F12.wireOp",EDGE,"E72.1");var subQ16=sQuery(id+"F12.wireOp",EDGE,"E74.1");var subQ18=sQuery(id+"F12.wireOp",EDGE,"E74.8");Q0=qUnion([makeQuery(id+"F12.imprint","IMPRINT",FACE,{"disambiguationData":[TD([[makeQuery(id+"F12.imprint","IMPRINT",EDGE,{"derivedFrom":subQ7}),1.0]])]}),makeQuery(id+"F12.imprint","IMPRINT",FACE,{"disambiguationData":[TD([[makeQuery(id+"F12.imprint","IMPRINT",EDGE,{"derivedFrom":subQ14}),1.0]])]}),makeQuery(id+"F12.imprint","IMPRINT",FACE,{"disambiguationData":[TD([[makeQuery(id+"F12.imprint","IMPRINT",EDGE,{"derivedFrom":subQ16}),1.0]])]}),makeQuery(id+"F12.imprint","IMPRINT",FACE,{"disambiguationData":[TD([[makeQuery(id+"F12.imprint","IMPRINT",EDGE,{"derivedFrom":subQ18}),-1.0]])]})]);}
            var Q1;
            Q1=makeQuery(id+"F5.boolean.opBoolean","SPLIT",FACE,{"disambiguationData":[TD([makeQuery(id+"F5.opExtrude","SWEPT_FACE",FACE,{"disambiguationData":[OSD([sQuery(id+"F4.wireOp",EDGE,"E41")])]})])],"derivedFrom":makeQuery(id+"F3.boolean.opBoolean","COPY",FACE,{"derivedFrom":makeQuery(id+"F3.opExtrude","CAP_FACE",FACE,{"disambiguationData":[OSD([sQuery(id+"F0.wireOp",EDGE,"E25.0"),sQuery(id+"F0.wireOp",EDGE,"E25.1"),sQuery(id+"F0.wireOp",EDGE,"E25.2"),sQuery(id+"F0.wireOp",EDGE,"E25.3"),sQuery(id+"F0.wireOp",EDGE,"E25.4"),sQuery(id+"F0.wireOp",EDGE,"E25.5"),sQuery(id+"F0.wireOp",EDGE,"E25.6"),sQuery(id+"F0.wireOp",EDGE,"E25.7")])],"isStart":false})})});
            extrude(context, id + "F13", {"entities" : qUnion([Q0]), "operationType" : NewBodyOperationType.REMOVE, "endBound" : BoundingType.UP_TO_SURFACE, "endBoundEntityFace" : qUnion([Q1]), "depth" : 25 * mm});
        }
        {
            var Q0;
            Q0=makeQuery(id+"F3.boolean.opBoolean","COPY",EDGE,{"derivedFrom":makeQuery(id+"F3.opExtrude","CAP_EDGE",EDGE,{"disambiguationData":[OSD([sQuery(id+"F0.wireOp",EDGE,"E25.6")])],"isStart":false})});
            var Q1;
            Q1=makeQuery(id+"F8.boolean.opBoolean","INTERSECT",EDGE,{"derivedFrom":[makeQuery(id+"F5.opExtrude","SWEPT_FACE",FACE,{"disambiguationData":[OSD([sQuery(id+"F4.wireOp",EDGE,"E30")])]}),makeQuery(id+"F8.opExtrude","CAP_FACE",FACE,{"disambiguationData":[OSD([sQuery(id+"F7.wireOp",EDGE,"E67")])],"isStart":false})]});
            var Q2;
            Q2=makeQuery(id+"F8.boolean.opBoolean","INTERSECT",EDGE,{"disambiguationData":[OD(1.0)],"derivedFrom":[makeQuery(id+"F5.opExtrude","SWEPT_FACE",FACE,{"disambiguationData":[OSD([sQuery(id+"F4.wireOp",EDGE,"E30")])]}),makeQuery(id+"F8.opExtrude","SWEPT_FACE",FACE,{"disambiguationData":[OSD([sQuery(id+"F7.wireOp",EDGE,"E67")])]})]});
            var Q3;
            {var subQ0=sQuery(id+"F4.wireOp",EDGE,"E30");Q3=makeQuery(id+"F8.boolean.opBoolean","SPLIT",EDGE,{"disambiguationData":[TD([makeQuery(id+"F5.opExtrude","SWEPT_FACE",FACE,{"disambiguationData":[OSD([sQuery(id+"F4.wireOp",EDGE,"E35.filletArc")])]})])],"derivedFrom":makeQuery(id+"F5.opExtrude","CAP_EDGE",EDGE,{"disambiguationData":[OSD([subQ0])],"isStart":false})});}
            var Q4;
            {var subQ0=sQuery(id+"F0.wireOp",EDGE,"E25.7");var subQ1=sQuery(id+"F0.wireOp",EDGE,"E25.1");var subQ2=sQuery(id+"F0.wireOp",EDGE,"E25.6");var subQ3=sQuery(id+"F0.wireOp",EDGE,"E25.5");var subQ4=sQuery(id+"F0.wireOp",EDGE,"E25.4");var subQ5=sQuery(id+"F0.wireOp",EDGE,"E25.0");var subQ6=sQuery(id+"F0.wireOp",EDGE,"E25.2");var subQ7=sQuery(id+"F0.wireOp",EDGE,"E25.3");Q4=makeQuery(id+"F8.boolean.opBoolean","INTERSECT",EDGE,{"derivedFrom":[makeQuery(id+"F5.boolean.opBoolean","SPLIT",FACE,{"disambiguationData":[TD([makeQuery(id+"F2.opExtrude","SWEPT_FACE",FACE,{"disambiguationData":[OSD([subQ5])]})])],"derivedFrom":makeQuery(id+"F3.boolean.opBoolean","COPY",FACE,{"derivedFrom":makeQuery(id+"F3.opExtrude","CAP_FACE",FACE,{"disambiguationData":[OSD([subQ5,subQ1,subQ6,subQ7,subQ4,subQ3,subQ2,subQ0])],"isStart":false})})}),makeQuery(id+"F8.opExtrude","SWEPT_FACE",FACE,{"disambiguationData":[OSD([sQuery(id+"F7.wireOp",EDGE,"E67")])]})]});}
            var Q5;
            Q5=makeQuery(id+"F8.boolean.opBoolean","INTERSECT",EDGE,{"disambiguationData":[OD(0.0)],"derivedFrom":[makeQuery(id+"F5.opExtrude","SWEPT_FACE",FACE,{"disambiguationData":[OSD([sQuery(id+"F4.wireOp",EDGE,"E30")])]}),makeQuery(id+"F8.opExtrude","SWEPT_FACE",FACE,{"disambiguationData":[OSD([sQuery(id+"F7.wireOp",EDGE,"E67")])]})]});
            fillet(context, id + "F14", {"entities" : qUnion([Q0, Q1, Q2, Q3, Q4, Q5]), "radius" : 3 * mm, "tangentPropagation" : true, "allowEdgeOverflow" : false});
        }
        {
            var Q0;
            Q0=makeQuery(id+"F1.opExtrude","CAP_EDGE",EDGE,{"disambiguationData":[OSD([sQuery(id+"F0.wireOp",EDGE,"E1.bottom")])],"isStart":false});
            fillet(context, id + "F15", {"entities" : qUnion([Q0]), "radius" : 2 * mm, "tangentPropagation" : true, "allowEdgeOverflow" : false});
        }
        {
            var Q0;
            {var subQ0=sQuery(id+"F0.wireOp",EDGE,"E21.filletArc");var subQ1=sQuery(id+"F0.wireOp",EDGE,"E7");var subQ2=sQuery(id+"F0.wireOp",EDGE,"E6");var subQ3=sQuery(id+"F0.wireOp",EDGE,"E5");var subQ4=sQuery(id+"F0.wireOp",EDGE,"E4");var subQ5=sQuery(id+"F0.wireOp",EDGE,"E22.filletArc");var subQ6=sQuery(id+"F0.wireOp",EDGE,"E1.bottom");var subQ7=sQuery(id+"F0.wireOp",EDGE,"E1.right");var subQ8=sQuery(id+"F0.wireOp",EDGE,"E1.top");var subQ9=sQuery(id+"F0.wireOp",EDGE,"E1.left");var subQ10=sQuery(id+"F0.wireOp",EDGE,"E23.filletArc");var subQ11=sQuery(id+"F0.wireOp",EDGE,"E24.filletArc");Q0=makeQuery(id+"F2.boolean.opBoolean","SPLIT",FACE,{"disambiguationData":[TD([makeQuery(id+"F1.opExtrude","SWEPT_FACE",FACE,{"disambiguationData":[OSD([subQ6])]})])],"derivedFrom":makeQuery(id+"F1.opExtrude","CAP_FACE",FACE,{"disambiguationData":[OSD([subQ6,subQ8,subQ9,subQ7,subQ4,subQ3,subQ2,subQ1,subQ0,subQ5,subQ10,subQ11])],"isStart":true})});}
            var sketch = newSketch(context, id + "F16", { "sketchPlane" : qUnion([Q0])});
            skPoint(sketch, "E79.endSnap0", {"position": v(1.26, 90) * mm});
            skCircle(sketch, "E80", {"center": v(1.26, 120) * mm, "radius": 6 * mm});
            skArc(sketch, "E81", {"start": v(16.26, 120) * mm, "mid": v(1.26, 135) * mm, "end": v(-13.74, 120) * mm});
            skLineSegment(sketch, "E82", {"start": v(-13.74, 120) * mm, "end": v(-13.74, 108) * mm});
            skLineSegment(sketch, "E83", {"start": v(-13.74, 108) * mm, "end": v(-31.74, 90) * mm});
            skLineSegment(sketch, "E84", {"start": v(16.26, 120) * mm, "end": v(16.26, 108) * mm});
            skLineSegment(sketch, "E85", {"start": v(16.26, 108) * mm, "end": v(34.26, 90) * mm});
            skPoint(sketch, "E86.MirrorP", {"position": v(1.26, 74.25) * mm});
            skArc(sketch, "E87.MirrorCS", {"start": v(-13.74, 120) * mm, "mid": v(1.26, 135) * mm, "end": v(16.26, 120) * mm});
            skPoint(sketch, "E88.MirrorP", {"position": v(0, 74.25) * mm});
            skPoint(sketch, "E89.endSnap0", {"position": v(80, 0) * mm});
            skLineSegment(sketch, "E90.MirrorCS", {"start": v(16.26, -120) * mm, "end": v(16.26, -108) * mm});
            skLineSegment(sketch, "E91.MirrorCS", {"start": v(-13.74, -120) * mm, "end": v(-13.74, -108) * mm});
            skLineSegment(sketch, "E92.MirrorCS", {"start": v(16.26, -108) * mm, "end": v(34.26, -90) * mm});
            skArc(sketch, "E93.MirrorCS", {"start": v(-13.74, -120) * mm, "mid": v(1.26, -135) * mm, "end": v(16.26, -120) * mm});
            skLineSegment(sketch, "E94.MirrorCS", {"start": v(-13.74, -108) * mm, "end": v(-31.74, -90) * mm});
            skPoint(sketch, "E95.MirrorP", {"position": v(1.26, -74.25) * mm});
            skCircle(sketch, "E96.MirrorC", {"center": v(1.26, -120) * mm, "radius": 6 * mm});
            skArc(sketch, "E97.MirrorCS", {"start": v(16.26, -120) * mm, "mid": v(1.26, -135) * mm, "end": v(-13.74, -120) * mm});
            skLineSegment(sketch, "E98", {"start": v(1.26, 90) * mm, "end": v(1.26, 120) * mm, "construction": true});
            skLineSegment(sketch, "E99", {"start": v(1.26, -74.25) * mm, "end": v(1.26, -104.25) * mm, "construction": true});
            skSolve(sketch);
        }
        {
            var Q0;
            Q0=makeQuery(id+"F16.imprint","IMPRINT",FACE,{"disambiguationData":[TD([[makeQuery(id+"F16.imprint","IMPRINT",EDGE,{"derivedFrom":sQuery(id+"F16.wireOp",EDGE,"E81")}),1.0]])]});
            var Q1;
            Q1=makeQuery(id+"F16.imprint","IMPRINT",FACE,{"disambiguationData":[TD([[makeQuery(id+"F16.imprint","IMPRINT",EDGE,{"derivedFrom":sQuery(id+"F16.wireOp",EDGE,"E91.MirrorCS")}),-1.0]])]});
            var Q2;
            Q2=makeQuery(id+"F16.imprint","IMPRINT",FACE,{"disambiguationData":[TD([[makeQuery(id+"F16.imprint","IMPRINT",EDGE,{"derivedFrom":makeQuery(id+"F1.opExtrude","CAP_EDGE",EDGE,{"disambiguationData":[OSD([sQuery(id+"F0.wireOp",EDGE,"E1.left")])],"isStart":true})}),-1.0]])]});
            var Q3;
            Q3=makeQuery(id+"F2.opExtrude","CAP_FACE",FACE,{"disambiguationData":[OSD([sQuery(id+"F0.wireOp",EDGE,"E12"),sQuery(id+"F0.wireOp",EDGE,"E13"),sQuery(id+"F0.wireOp",EDGE,"E14"),sQuery(id+"F0.wireOp",EDGE,"E15"),sQuery(id+"F0.wireOp",EDGE,"E17.filletArc"),sQuery(id+"F0.wireOp",EDGE,"E18.filletArc"),sQuery(id+"F0.wireOp",EDGE,"E19.filletArc"),sQuery(id+"F0.wireOp",EDGE,"E20.filletArc"),sQuery(id+"F0.wireOp",EDGE,"E25.0"),sQuery(id+"F0.wireOp",EDGE,"E25.1"),sQuery(id+"F0.wireOp",EDGE,"E25.2"),sQuery(id+"F0.wireOp",EDGE,"E25.3"),sQuery(id+"F0.wireOp",EDGE,"E25.4"),sQuery(id+"F0.wireOp",EDGE,"E25.5"),sQuery(id+"F0.wireOp",EDGE,"E25.6"),sQuery(id+"F0.wireOp",EDGE,"E25.7")])],"isStart":false});
            extrude(context, id + "F17", {"entities" : qUnion([Q0, Q1, Q2]), "endBound" : BoundingType.UP_TO_SURFACE, "endBoundEntityFace" : qUnion([Q3]), "depth" : 25 * mm});
        }
    });
